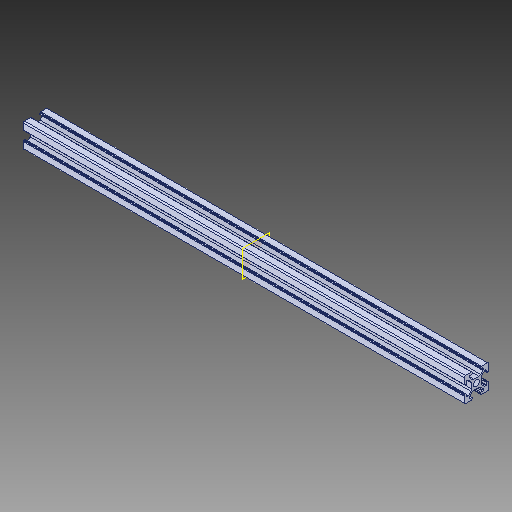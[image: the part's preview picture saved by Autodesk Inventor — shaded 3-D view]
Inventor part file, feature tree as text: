
AUTODESK INVENTOR PART (.ipt)
format: ipt  version: 2018 (Build 220112000, 112)  size: 376,320 bytes
history: native  units: in
note: dims shown in document units (in); Inventor stores cm internally (conversion verified against a paired STEP export)
features: extrude x1, plane x1, sketch x1, projected_geometry x1, fillet x1
ambient origin geometry x8: Origin, YZ Plane, XZ Plane, XY Plane, X Axis, Y Axis, Z Axis, Center Point
bodies: Solid1 (feature_tree)
feature tree (5):
  extrude  "Extrusion2"  [1 undecoded]
  plane  "Work Plane1"
  sketch  "Sketch3"  dims[d2=10.2362in d3=0.0in]
  projected_geometry  "Projected Loop2"
  fillet  "Fillet5"  [1 undecoded]
note: 2 required parameter values undecoded (feature->parameter linkage not recoverable at this tier; creation-order binding heuristic only, values carry confidence <= 0.55)
